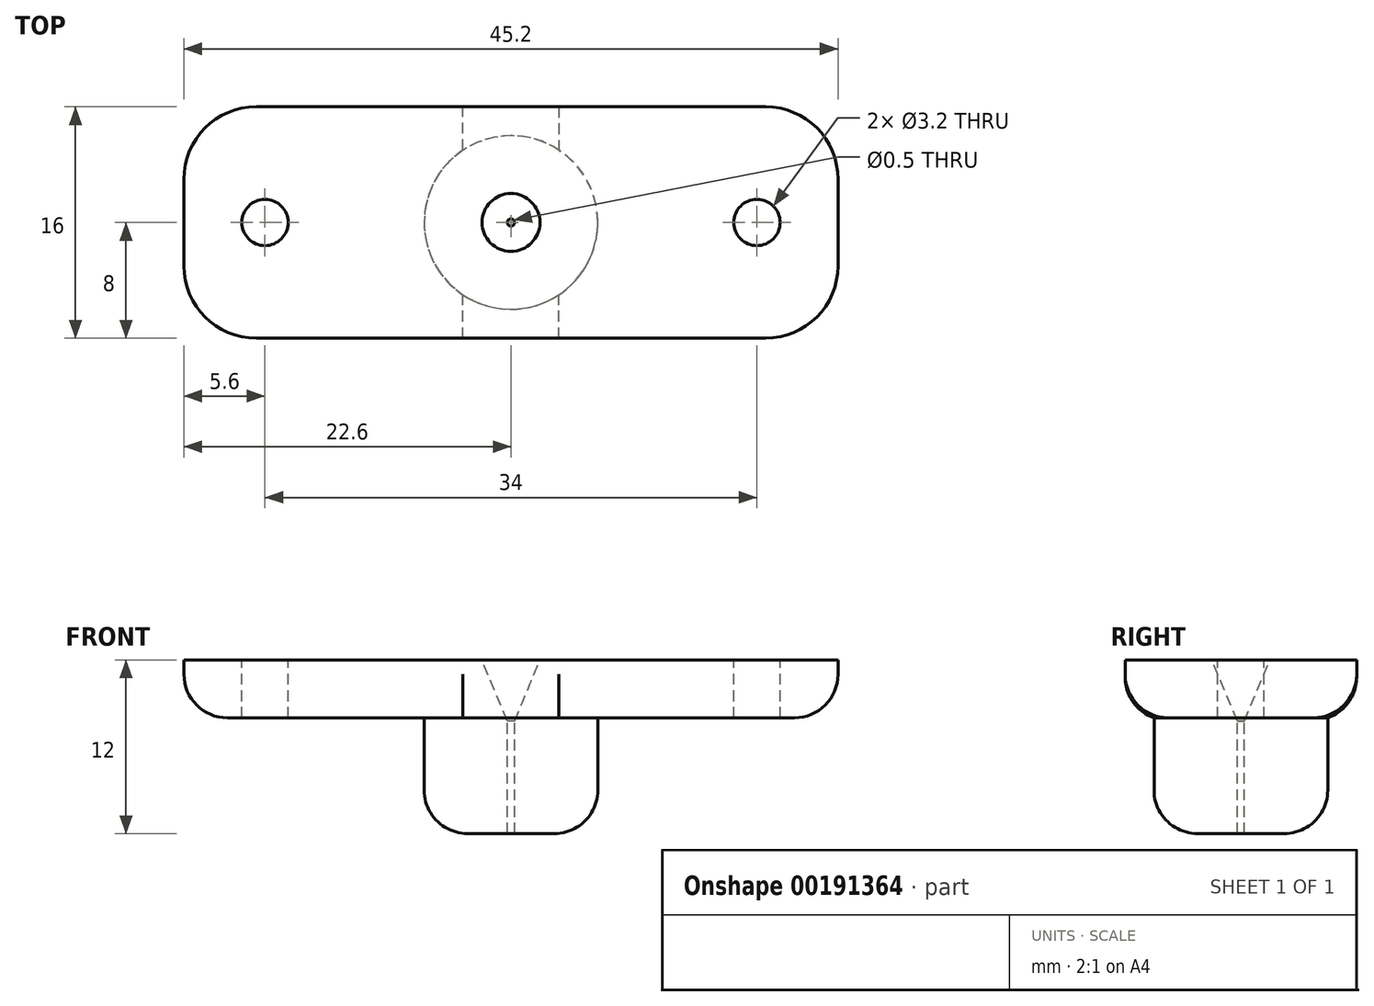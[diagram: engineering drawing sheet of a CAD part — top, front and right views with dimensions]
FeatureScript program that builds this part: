
annotation { "Feature Type Name" : "Feature", "Feature Type Description" : "" }
export const myFeature = defineFeature(function(context is Context, id is Id, definition is map)
    precondition{}
    {
        {
            var Q0;
            Q0=qCreatedBy(makeId("Top.planeOp"),FACE);
            var sketch = newSketch(context, id + "F0", { "sketchPlane" : qUnion([Q0])});
            skCircle(sketch, "E0", {"center": v(0, 0) * mm, "radius": 4 * mm});
            skLineSegment(sketch, "E1", {"start": v(-17, 0) * mm, "end": v(17, 0) * mm, "construction": true});
            skCircle(sketch, "E2", {"center": v(-17, 0) * mm, "radius": 1.6 * mm});
            skCircle(sketch, "E3", {"center": v(17, 0) * mm, "radius": 1.6 * mm});
            skLineSegment(sketch, "E4.bottom", {"start": v(17.6, 8) * mm, "end": v(-17.6, 8) * mm});
            skLineSegment(sketch, "E4.top", {"start": v(17.6, -8) * mm, "end": v(-17.6, -8) * mm});
            skLineSegment(sketch, "E4.left", {"start": v(22.6, 3) * mm, "end": v(22.6, -3) * mm});
            skLineSegment(sketch, "E4.right", {"start": v(-22.6, 3) * mm, "end": v(-22.6, -3) * mm});
            skPoint(sketch, "E5.visualSharp", {"position": v(-22.6, -8) * mm});
            skArc(sketch, "E5.filletArc", {"start": v(-22.6, -3) * mm, "mid": v(-21.14, -6.54) * mm, "end": v(-17.6, -8) * mm});
            skPoint(sketch, "E6.visualSharp", {"position": v(-22.6, 8) * mm});
            skArc(sketch, "E6.filletArc", {"start": v(-17.6, 8) * mm, "mid": v(-21.14, 6.54) * mm, "end": v(-22.6, 3) * mm});
            skPoint(sketch, "E7.visualSharp", {"position": v(22.6, 8) * mm});
            skArc(sketch, "E7.filletArc", {"start": v(22.6, 3) * mm, "mid": v(21.14, 6.54) * mm, "end": v(17.6, 8) * mm});
            skPoint(sketch, "E8.visualSharp", {"position": v(22.6, -8) * mm});
            skArc(sketch, "E8.filletArc", {"start": v(17.6, -8) * mm, "mid": v(21.14, -6.54) * mm, "end": v(22.6, -3) * mm});
            skCircle(sketch, "E9", {"center": v(0, 0) * mm, "radius": 6 * mm});
            skSolve(sketch);
        }
        {
            var Q0;
            Q0=makeQuery(id+"F0.imprint","IMPRINT",FACE,{"disambiguationData":[TD([[makeQuery(id+"F0.imprint","IMPRINT",EDGE,{"derivedFrom":sQuery(id+"F0.wireOp",EDGE,"E2")}),-1.0]])]});
            var Q1;
            Q1=makeQuery(id+"F0.imprint","IMPRINT",FACE,{"disambiguationData":[TD([[makeQuery(id+"F0.imprint","IMPRINT",EDGE,{"derivedFrom":sQuery(id+"F0.wireOp",EDGE,"E0")}),-1.0]])]});
            var Q2;
            Q2=makeQuery(id+"F0.imprint","IMPRINT",FACE,{"disambiguationData":[TD([[makeQuery(id+"F0.imprint","IMPRINT",EDGE,{"derivedFrom":sQuery(id+"F0.wireOp",EDGE,"E0")}),1.0]])]});
            extrude(context, id + "F1", {"entities" : qUnion([Q0, Q1, Q2]), "oppositeDirection" : true, "depth" : 4 * mm});
        }
        {
            var Q0;
            Q0=makeQuery(id+"F0.imprint","IMPRINT",FACE,{"disambiguationData":[TD([[makeQuery(id+"F0.imprint","IMPRINT",EDGE,{"derivedFrom":sQuery(id+"F0.wireOp",EDGE,"E0")}),-1.0]])]});
            var Q1;
            Q1=makeQuery(id+"F0.imprint","IMPRINT",FACE,{"disambiguationData":[TD([[makeQuery(id+"F0.imprint","IMPRINT",EDGE,{"derivedFrom":sQuery(id+"F0.wireOp",EDGE,"E0")}),1.0]])]});
            extrude(context, id + "F2", {"entities" : qUnion([Q0, Q1]), "operationType" : NewBodyOperationType.ADD, "oppositeDirection" : true, "depth" : 12 * mm});
        }
        {
            var Q0;
            Q0=sQuery(id+"F0.wireOp",VERTEX,"E0.center");
            var Q1;
            Q1=makeQuery(id+"F1.opExtrude","SWEPT_BODY",BODY,{"disambiguationData":[OSD([sQuery(id+"F0.wireOp",EDGE,"E2"),sQuery(id+"F0.wireOp",EDGE,"E3"),sQuery(id+"F0.wireOp",EDGE,"E4.bottom"),sQuery(id+"F0.wireOp",EDGE,"E4.top"),sQuery(id+"F0.wireOp",EDGE,"E4.left"),sQuery(id+"F0.wireOp",EDGE,"E4.right"),sQuery(id+"F0.wireOp",EDGE,"E5.filletArc"),sQuery(id+"F0.wireOp",EDGE,"E6.filletArc"),sQuery(id+"F0.wireOp",EDGE,"E7.filletArc"),sQuery(id+"F0.wireOp",EDGE,"E8.filletArc")])]});
            hole(context, id + "F3", {"style" : HoleStyle.C_SINK, "endStyle" : HoleEndStyle.THROUGH, "holeDiameter" : .5 * mm, "cSinkDiameter" : 4 * mm, "cSinkAngle" : 45 * degree, "locations" : qUnion([Q0]), "scope" : qUnion([Q1]), "isTappedThrough" : true});
        }
        {
            var Q0;
            Q0=makeQuery(id+"F1.opExtrude","CAP_EDGE",EDGE,{"disambiguationData":[OSD([sQuery(id+"F0.wireOp",EDGE,"E8.filletArc")])],"isStart":false});
            var Q1;
            Q1=makeQuery(id+"F2.opExtrude","CAP_EDGE",EDGE,{"disambiguationData":[OSD([sQuery(id+"F0.wireOp",EDGE,"E9")])],"isStart":false});
            fillet(context, id + "F4", {"entities" : qUnion([Q0, Q1]), "radius" : 3 * mm, "tangentPropagation" : true, "allowEdgeOverflow" : false});
        }
    });
